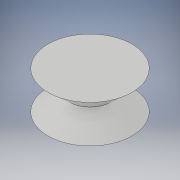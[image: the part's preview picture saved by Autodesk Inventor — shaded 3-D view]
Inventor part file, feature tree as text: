
AUTODESK INVENTOR PART (.ipt)
format: ipt  version: 2019 (Build 230136000, 136)  size: 103,424 bytes
history: native  units: in
note: dims shown in document units (in); Inventor stores cm internally (conversion verified against a paired STEP export)
features: sketch x2, plane x1, loft x1, mirror x1
ambient origin geometry x8: Origin, YZ Plane, XZ Plane, XY Plane, X Axis, Y Axis, Z Axis, Center Point
bodies: Solid1 (feature_tree)
feature tree (5):
  sketch  "Sketch1"  dims[d0=1.0in d1=0.45in]
  plane  "Work Plane1"
  loft  "Loft1"
  mirror  "Mirror1"
  sketch  "Sketch2"  dims[d2=2.0in d3=0.0in d4=90.0deg d5=0.0in d6=90.0deg]
